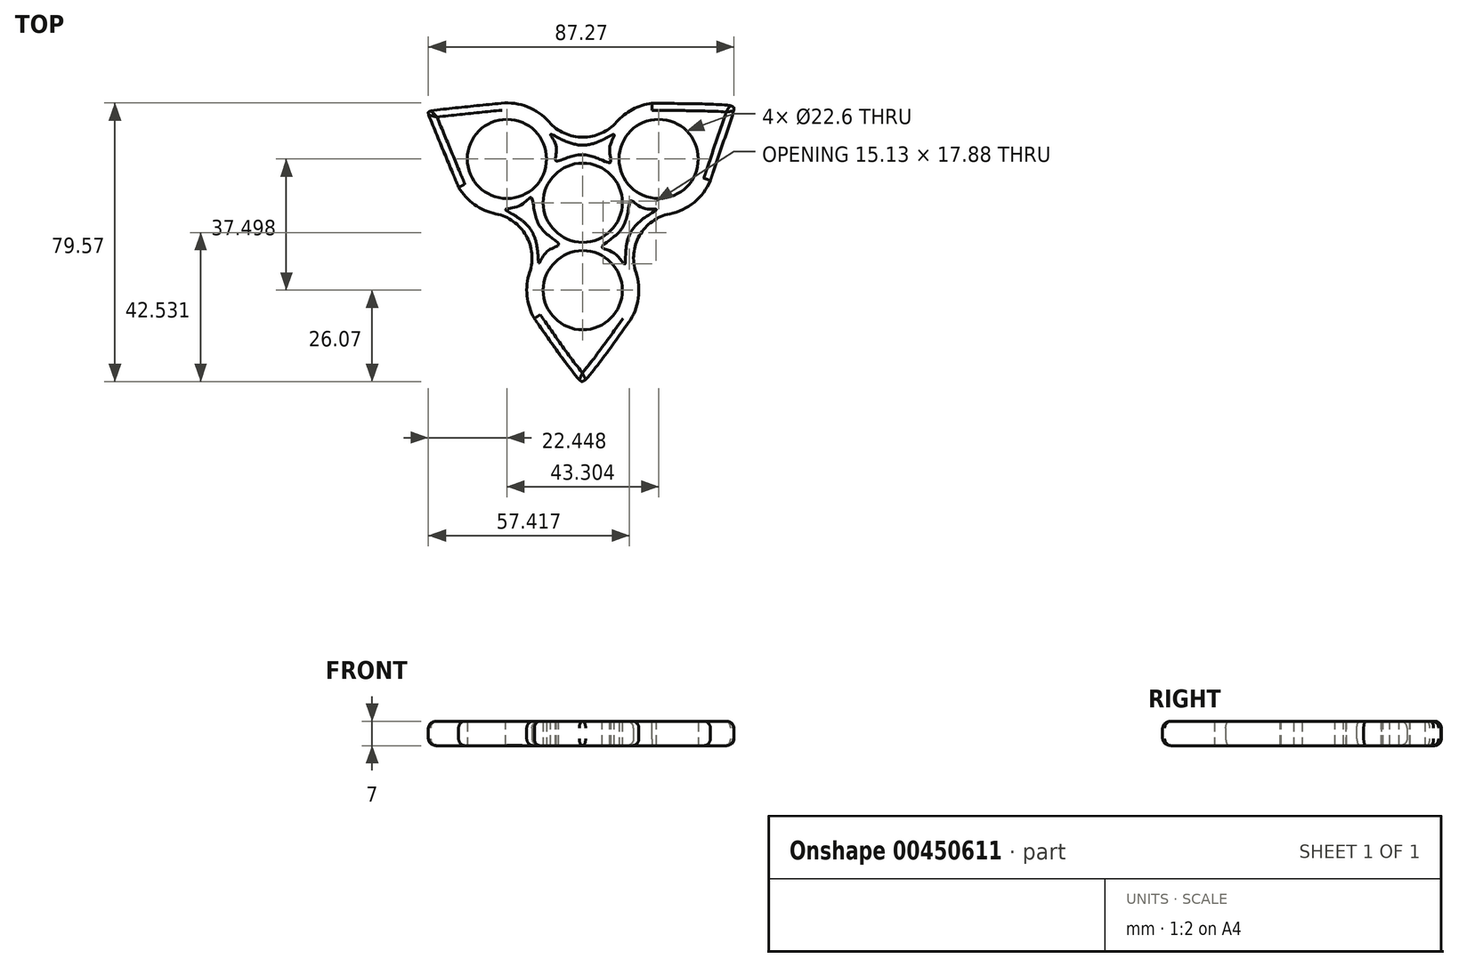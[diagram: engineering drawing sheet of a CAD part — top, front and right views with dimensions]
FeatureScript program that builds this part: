
annotation { "Feature Type Name" : "Feature", "Feature Type Description" : "" }
export const myFeature = defineFeature(function(context is Context, id is Id, definition is map)
    precondition{}
    {
        {
            var Q0;
            Q0=qCreatedBy(makeId("Top.planeOp"),FACE);
            var sketch = newSketch(context, id + "F0", { "sketchPlane" : qUnion([Q0])});
            skCircle(sketch, "E0", {"center": v(0, 0) * mm, "radius": 25 * mm});
            skCircle(sketch, "E1", {"center": v(0, 0) * mm, "radius": 11.3 * mm});
            skCircle(sketch, "E2", {"center": v(21.65, 12.5) * mm, "radius": 11.3 * mm});
            skCircle(sketch, "E3", {"center": v(-21.65, 12.5) * mm, "radius": 11.3 * mm});
            skCircle(sketch, "E4", {"center": v(0, -25) * mm, "radius": 11.3 * mm});
            skCircle(sketch, "E5", {"center": v(21.65, 12.5) * mm, "radius": 16 * mm});
            skCircle(sketch, "E6", {"center": v(-21.65, 12.5) * mm, "radius": 16 * mm});
            skCircle(sketch, "E7", {"center": v(0, -25) * mm, "radius": 16 * mm});
            skArc(sketch, "E8", {"start": v(-9.64, 23.07) * mm, "mid": v(0, 18.7) * mm, "end": v(9.64, 23.07) * mm});
            skArc(sketch, "E9", {"start": v(-15.16, -19.88) * mm, "mid": v(-16.2, -9.36) * mm, "end": v(-24.8, -3.2) * mm});
            skArc(sketch, "E10", {"start": v(24.8, -3.2) * mm, "mid": v(16.2, -9.36) * mm, "end": v(15.16, -19.88) * mm});
            skFitSpline(sketch, "E11", {"points": [v(-35.44, 4.38) * mm, v(-44.09, 25.63) * mm, v(-23.28, 28.41) * mm], "startDerivative": vector(-46.1, 111.22) * mm, "endDerivative": vector(124.83, 12.76) * mm});
            skFitSpline(sketch, "E12", {"points": [v(19.7, 28.38) * mm, v(43.05, 27.27) * mm, v(36.41, 6.32) * mm], "startDerivative": vector(126.76, -0.4) * mm, "endDerivative": vector(-40.32, -120.34) * mm});
            skFitSpline(sketch, "E13", {"points": [v(-13.83, -33.05) * mm, v(0, -51) * mm, v(13.08, -34.21) * mm], "startDerivative": vector(77.66, -112.58) * mm, "endDerivative": vector(73.36, 104.16) * mm});
            skFitSpline(sketch, "E14", {"points": [v(-9.15, 19.56) * mm, v(-7.58, 15.99) * mm, v(-7.67, 11.98) * mm, v(0, 13.72) * mm, v(7.85, 11.46) * mm, v(7.67, 15.55) * mm, v(8.9, 19.47) * mm, v(0, 16.42) * mm, v(-9.15, 19.56) * mm]});
            skFitSpline(sketch, "E15", {"points": [v(21.04, -1.96) * mm, v(17.17, -1.53) * mm, v(13.74, 0.55) * mm, v(11.41, -6.96) * mm, v(5.53, -12.62) * mm, v(9.16, -14.52) * mm, v(11.95, -17.54) * mm, v(13.75, -8.31) * mm, v(21.04, -1.96) * mm]});
            skFitSpline(sketch, "E16", {"points": [v(-12.51, -17.25) * mm, v(-10.33, -14.02) * mm, v(-6.9, -11.95) * mm, v(-12.46, -6.4) * mm, v(-14.73, 1.44) * mm, v(-18.1, -0.89) * mm, v(-22.07, -1.95) * mm, v(-14.74, -7.84) * mm, v(-12.51, -17.25) * mm]});
            skSolve(sketch);
        }
        {
            var Q0;
            {var subQ4=sQuery(id+"F0.wireOp",EDGE,"E6");var subQ5=sQuery(id+"F0.wireOp",EDGE,"E1");var subQ6=makeQuery(id+"F0.imprint","INTERSECT",VERTEX,{"disambiguationData":[OD(0.0)],"derivedFrom":[subQ5,subQ4]});Q0=makeQuery(id+"F0.imprint","IMPRINT",FACE,{"disambiguationData":[TD([[makeQuery(id+"F0.imprint","IMPRINT",EDGE,{"disambiguationData":[TD([[subQ6,-1.0]])],"derivedFrom":subQ5}),-1.0]])]});}
            var Q1;
            {var subQ0=sQuery(id+"F0.wireOp",EDGE,"E5");var subQ1=sQuery(id+"F0.wireOp",EDGE,"E1");var subQ2=makeQuery(id+"F0.imprint","INTERSECT",VERTEX,{"disambiguationData":[OD(0.0)],"derivedFrom":[subQ1,subQ0]});Q1=makeQuery(id+"F0.imprint","IMPRINT",FACE,{"disambiguationData":[TD([[makeQuery(id+"F0.imprint","IMPRINT",EDGE,{"disambiguationData":[TD([[subQ2,-1.0]])],"derivedFrom":subQ1}),-1.0]])]});}
            var Q2;
            {var subQ4=sQuery(id+"F0.wireOp",EDGE,"E5");var subQ5=sQuery(id+"F0.wireOp",EDGE,"E1");var subQ6=makeQuery(id+"F0.imprint","INTERSECT",VERTEX,{"disambiguationData":[OD(0.0)],"derivedFrom":[subQ5,subQ4]});Q2=makeQuery(id+"F0.imprint","IMPRINT",FACE,{"disambiguationData":[TD([[makeQuery(id+"F0.imprint","IMPRINT",EDGE,{"disambiguationData":[TD([[subQ6,1.0]])],"derivedFrom":subQ5}),-1.0]])]});}
            var Q3;
            {var subQ1=sQuery(id+"F0.wireOp",EDGE,"E0");var subQ3=sQuery(id+"F0.wireOp",EDGE,"E2");var subQ4=makeQuery(id+"F0.imprint","INTERSECT",VERTEX,{"disambiguationData":[OD(0.0)],"derivedFrom":[subQ1,subQ3]});Q3=makeQuery(id+"F0.imprint","IMPRINT",FACE,{"disambiguationData":[TD([[makeQuery(id+"F0.imprint","IMPRINT",EDGE,{"disambiguationData":[TD([[subQ4,1.0]])],"derivedFrom":subQ3}),-1.0]])]});}
            var Q4;
            {var subQ0=sQuery(id+"F0.wireOp",EDGE,"E5");var subQ1=sQuery(id+"F0.wireOp",EDGE,"E1");var subQ2=makeQuery(id+"F0.imprint","INTERSECT",VERTEX,{"disambiguationData":[OD(1.0)],"derivedFrom":[subQ1,subQ0]});Q4=makeQuery(id+"F0.imprint","IMPRINT",FACE,{"disambiguationData":[TD([[makeQuery(id+"F0.imprint","IMPRINT",EDGE,{"disambiguationData":[TD([[subQ2,1.0]])],"derivedFrom":subQ1}),-1.0]])]});}
            var Q5;
            {var subQ0=sQuery(id+"F0.wireOp",EDGE,"E7");var subQ1=sQuery(id+"F0.wireOp",EDGE,"E1");var subQ2=makeQuery(id+"F0.imprint","INTERSECT",VERTEX,{"disambiguationData":[OD(0.0)],"derivedFrom":[subQ1,subQ0]});Q5=makeQuery(id+"F0.imprint","IMPRINT",FACE,{"disambiguationData":[TD([[makeQuery(id+"F0.imprint","IMPRINT",EDGE,{"disambiguationData":[TD([[subQ2,-1.0]])],"derivedFrom":subQ1}),-1.0]])]});}
            var Q6;
            {var subQ0=sQuery(id+"F0.wireOp",EDGE,"E6");var subQ1=sQuery(id+"F0.wireOp",EDGE,"E1");var subQ2=makeQuery(id+"F0.imprint","INTERSECT",VERTEX,{"disambiguationData":[OD(1.0)],"derivedFrom":[subQ1,subQ0]});Q6=makeQuery(id+"F0.imprint","IMPRINT",FACE,{"disambiguationData":[TD([[makeQuery(id+"F0.imprint","IMPRINT",EDGE,{"disambiguationData":[TD([[subQ2,-1.0]])],"derivedFrom":subQ1}),-1.0]])]});}
            var Q7;
            {var subQ1=sQuery(id+"F0.wireOp",EDGE,"E0");var subQ3=sQuery(id+"F0.wireOp",EDGE,"E3");var subQ4=makeQuery(id+"F0.imprint","INTERSECT",VERTEX,{"disambiguationData":[OD(0.0)],"derivedFrom":[subQ1,subQ3]});Q7=makeQuery(id+"F0.imprint","IMPRINT",FACE,{"disambiguationData":[TD([[makeQuery(id+"F0.imprint","IMPRINT",EDGE,{"disambiguationData":[TD([[subQ4,-1.0]])],"derivedFrom":subQ3}),-1.0]])]});}
            var Q8;
            {var subQ1=sQuery(id+"F0.wireOp",EDGE,"E0");var subQ3=sQuery(id+"F0.wireOp",EDGE,"E4");var subQ4=makeQuery(id+"F0.imprint","INTERSECT",VERTEX,{"disambiguationData":[OD(0.0)],"derivedFrom":[subQ1,subQ3]});Q8=makeQuery(id+"F0.imprint","IMPRINT",FACE,{"disambiguationData":[TD([[makeQuery(id+"F0.imprint","IMPRINT",EDGE,{"disambiguationData":[TD([[subQ4,-1.0]])],"derivedFrom":subQ3}),-1.0]])]});}
            var Q9;
            {var subQ0=sQuery(id+"F0.wireOp",EDGE,"E11");var subQ1=sQuery(id+"F0.wireOp",EDGE,"E6");var subQ2=makeQuery(id+"F0.imprint","INTERSECT",VERTEX,{"disambiguationData":[OD(2.0)],"derivedFrom":[subQ1,subQ0]});Q9=makeQuery(id+"F0.imprint","IMPRINT",FACE,{"disambiguationData":[TD([[makeQuery(id+"F0.imprint","IMPRINT",EDGE,{"disambiguationData":[TD([[subQ2,-1.0]])],"derivedFrom":subQ1}),-1.0]])]});}
            var Q10;
            {var subQ0=sQuery(id+"F0.wireOp",EDGE,"E12");var subQ1=sQuery(id+"F0.wireOp",EDGE,"E5");var subQ2=makeQuery(id+"F0.imprint","INTERSECT",VERTEX,{"disambiguationData":[OD(2.0)],"derivedFrom":[subQ1,subQ0]});Q10=makeQuery(id+"F0.imprint","IMPRINT",FACE,{"disambiguationData":[TD([[makeQuery(id+"F0.imprint","IMPRINT",EDGE,{"disambiguationData":[TD([[subQ2,1.0]])],"derivedFrom":subQ1}),-1.0]])]});}
            var Q11;
            {var subQ0=sQuery(id+"F0.wireOp",EDGE,"E11");var subQ1=sQuery(id+"F0.wireOp",EDGE,"E6");var subQ2=makeQuery(id+"F0.imprint","INTERSECT",VERTEX,{"disambiguationData":[OD(1.0)],"derivedFrom":[subQ1,subQ0]});Q11=makeQuery(id+"F0.imprint","IMPRINT",FACE,{"disambiguationData":[TD([[makeQuery(id+"F0.imprint","IMPRINT",EDGE,{"disambiguationData":[TD([[subQ2,-1.0]])],"derivedFrom":subQ1}),-1.0]])]});}
            var Q12;
            {var subQ0=sQuery(id+"F0.wireOp",EDGE,"E13");var subQ1=sQuery(id+"F0.wireOp",EDGE,"E7");var subQ2=makeQuery(id+"F0.imprint","INTERSECT",VERTEX,{"disambiguationData":[OD(1.0)],"derivedFrom":[subQ1,subQ0]});Q12=makeQuery(id+"F0.imprint","IMPRINT",FACE,{"disambiguationData":[TD([[makeQuery(id+"F0.imprint","IMPRINT",EDGE,{"disambiguationData":[TD([[subQ2,1.0]])],"derivedFrom":subQ1}),-1.0]])]});}
            var Q13;
            {var subQ0=sQuery(id+"F0.wireOp",EDGE,"E8");Q13=makeQuery(id+"F0.imprint","IMPRINT",FACE,{"disambiguationData":[TD([[makeQuery(id+"F0.imprint","IMPRINT",EDGE,{"derivedFrom":subQ0}),-1.0]])]});}
            var Q14;
            {var subQ0=sQuery(id+"F0.wireOp",EDGE,"E10");Q14=makeQuery(id+"F0.imprint","IMPRINT",FACE,{"disambiguationData":[TD([[makeQuery(id+"F0.imprint","IMPRINT",EDGE,{"derivedFrom":subQ0}),-1.0]])]});}
            var Q15;
            {var subQ0=sQuery(id+"F0.wireOp",EDGE,"E9");Q15=makeQuery(id+"F0.imprint","IMPRINT",FACE,{"disambiguationData":[TD([[makeQuery(id+"F0.imprint","IMPRINT",EDGE,{"derivedFrom":subQ0}),-1.0]])]});}
            extrude(context, id + "F1", {"entities" : qUnion([Q0, Q1, Q2, Q3, Q4, Q5, Q6, Q7, Q8, Q9, Q10, Q11, Q12, Q13, Q14, Q15]), "depth" : 7 * mm});
        }
        {
            var Q0;
            Q0=makeQuery(id+"F1.opExtrude","CAP_EDGE",EDGE,{"disambiguationData":[OSD([sQuery(id+"F0.wireOp",EDGE,"E13")])],"isStart":false});
            var Q1;
            {var subQ0=sQuery(id+"F0.wireOp",EDGE,"E7");Q1=makeQuery(id+"F1.opExtrude","CAP_EDGE",EDGE,{"disambiguationData":[OSD([subQ0]),TDD([makeQuery(id+"F0.imprint","IMPRINT",EDGE,{"disambiguationData":[TD([[makeQuery(id+"F0.imprint","INTERSECT",VERTEX,{"disambiguationData":[OD(1.0)],"derivedFrom":[subQ0,sQuery(id+"F0.wireOp",EDGE,"E13")]}),-1.0]])],"derivedFrom":subQ0})])],"isStart":false});}
            var Q2;
            Q2=makeQuery(id+"F1.opExtrude","CAP_EDGE",EDGE,{"disambiguationData":[OSD([sQuery(id+"F0.wireOp",EDGE,"E10")])],"isStart":false});
            var Q3;
            {var subQ0=sQuery(id+"F0.wireOp",EDGE,"E5");Q3=makeQuery(id+"F1.opExtrude","CAP_EDGE",EDGE,{"disambiguationData":[OSD([subQ0]),TDD([makeQuery(id+"F0.imprint","IMPRINT",EDGE,{"disambiguationData":[TD([[makeQuery(id+"F0.imprint","INTERSECT",VERTEX,{"disambiguationData":[OD(1.0)],"derivedFrom":[subQ0,sQuery(id+"F0.wireOp",EDGE,"E12")]}),1.0]])],"derivedFrom":subQ0})])],"isStart":false});}
            var Q4;
            Q4=makeQuery(id+"F1.opExtrude","CAP_EDGE",EDGE,{"disambiguationData":[OSD([sQuery(id+"F0.wireOp",EDGE,"E12")])],"isStart":false});
            var Q5;
            {var subQ0=sQuery(id+"F0.wireOp",EDGE,"E5");Q5=makeQuery(id+"F1.opExtrude","CAP_EDGE",EDGE,{"disambiguationData":[OSD([subQ0]),TDD([makeQuery(id+"F0.imprint","IMPRINT",EDGE,{"disambiguationData":[TD([[makeQuery(id+"F0.imprint","INTERSECT",VERTEX,{"disambiguationData":[OD(0.0)],"derivedFrom":[subQ0,sQuery(id+"F0.wireOp",EDGE,"E12")]}),-1.0]])],"derivedFrom":subQ0})])],"isStart":false});}
            var Q6;
            Q6=makeQuery(id+"F1.opExtrude","CAP_EDGE",EDGE,{"disambiguationData":[OSD([sQuery(id+"F0.wireOp",EDGE,"E8")])],"isStart":false});
            var Q7;
            {var subQ0=sQuery(id+"F0.wireOp",EDGE,"E6");Q7=makeQuery(id+"F1.opExtrude","CAP_EDGE",EDGE,{"disambiguationData":[OSD([subQ0]),TDD([makeQuery(id+"F0.imprint","IMPRINT",EDGE,{"disambiguationData":[TD([[makeQuery(id+"F0.imprint","INTERSECT",VERTEX,{"disambiguationData":[OD(1.0)],"derivedFrom":[subQ0,sQuery(id+"F0.wireOp",EDGE,"E11")]}),1.0]])],"derivedFrom":subQ0})])],"isStart":false});}
            var Q8;
            Q8=makeQuery(id+"F1.opExtrude","CAP_EDGE",EDGE,{"disambiguationData":[OSD([sQuery(id+"F0.wireOp",EDGE,"E11")])],"isStart":false});
            var Q9;
            {var subQ0=sQuery(id+"F0.wireOp",EDGE,"E6");Q9=makeQuery(id+"F1.opExtrude","CAP_EDGE",EDGE,{"disambiguationData":[OSD([subQ0]),TDD([makeQuery(id+"F0.imprint","IMPRINT",EDGE,{"disambiguationData":[TD([[makeQuery(id+"F0.imprint","INTERSECT",VERTEX,{"disambiguationData":[OD(0.0)],"derivedFrom":[subQ0,sQuery(id+"F0.wireOp",EDGE,"E11")]}),-1.0]])],"derivedFrom":subQ0})])],"isStart":false});}
            var Q10;
            Q10=makeQuery(id+"F1.opExtrude","CAP_EDGE",EDGE,{"disambiguationData":[OSD([sQuery(id+"F0.wireOp",EDGE,"E9")])],"isStart":false});
            var Q11;
            {var subQ0=sQuery(id+"F0.wireOp",EDGE,"E7");Q11=makeQuery(id+"F1.opExtrude","CAP_EDGE",EDGE,{"disambiguationData":[OSD([subQ0]),TDD([makeQuery(id+"F0.imprint","IMPRINT",EDGE,{"disambiguationData":[TD([[makeQuery(id+"F0.imprint","INTERSECT",VERTEX,{"disambiguationData":[OD(0.0)],"derivedFrom":[subQ0,sQuery(id+"F0.wireOp",EDGE,"E13")]}),1.0]])],"derivedFrom":subQ0})])],"isStart":false});}
            fillet(context, id + "F2", {"entities" : qUnion([Q0, Q1, Q2, Q3, Q4, Q5, Q6, Q7, Q8, Q9, Q10, Q11]), "radius" : 2 * mm, "tangentPropagation" : true, "allowEdgeOverflow" : false});
        }
        {
            var Q0;
            Q0=makeQuery(id+"F1.opExtrude","CAP_EDGE",EDGE,{"disambiguationData":[OSD([sQuery(id+"F0.wireOp",EDGE,"E13")])],"isStart":true});
            var Q1;
            {var subQ0=sQuery(id+"F0.wireOp",EDGE,"E7");Q1=makeQuery(id+"F1.opExtrude","CAP_EDGE",EDGE,{"disambiguationData":[OSD([subQ0]),TDD([makeQuery(id+"F0.imprint","IMPRINT",EDGE,{"disambiguationData":[TD([[makeQuery(id+"F0.imprint","INTERSECT",VERTEX,{"disambiguationData":[OD(0.0)],"derivedFrom":[subQ0,sQuery(id+"F0.wireOp",EDGE,"E13")]}),1.0]])],"derivedFrom":subQ0})])],"isStart":true});}
            var Q2;
            Q2=makeQuery(id+"F1.opExtrude","CAP_EDGE",EDGE,{"disambiguationData":[OSD([sQuery(id+"F0.wireOp",EDGE,"E9")])],"isStart":true});
            var Q3;
            {var subQ0=sQuery(id+"F0.wireOp",EDGE,"E6");Q3=makeQuery(id+"F1.opExtrude","CAP_EDGE",EDGE,{"disambiguationData":[OSD([subQ0]),TDD([makeQuery(id+"F0.imprint","IMPRINT",EDGE,{"disambiguationData":[TD([[makeQuery(id+"F0.imprint","INTERSECT",VERTEX,{"disambiguationData":[OD(0.0)],"derivedFrom":[subQ0,sQuery(id+"F0.wireOp",EDGE,"E11")]}),-1.0]])],"derivedFrom":subQ0})])],"isStart":true});}
            var Q4;
            Q4=makeQuery(id+"F1.opExtrude","CAP_EDGE",EDGE,{"disambiguationData":[OSD([sQuery(id+"F0.wireOp",EDGE,"E11")])],"isStart":true});
            var Q5;
            {var subQ0=sQuery(id+"F0.wireOp",EDGE,"E6");Q5=makeQuery(id+"F1.opExtrude","CAP_EDGE",EDGE,{"disambiguationData":[OSD([subQ0]),TDD([makeQuery(id+"F0.imprint","IMPRINT",EDGE,{"disambiguationData":[TD([[makeQuery(id+"F0.imprint","INTERSECT",VERTEX,{"disambiguationData":[OD(1.0)],"derivedFrom":[subQ0,sQuery(id+"F0.wireOp",EDGE,"E11")]}),1.0]])],"derivedFrom":subQ0})])],"isStart":true});}
            var Q6;
            Q6=makeQuery(id+"F1.opExtrude","CAP_EDGE",EDGE,{"disambiguationData":[OSD([sQuery(id+"F0.wireOp",EDGE,"E8")])],"isStart":true});
            var Q7;
            {var subQ0=sQuery(id+"F0.wireOp",EDGE,"E5");Q7=makeQuery(id+"F1.opExtrude","CAP_EDGE",EDGE,{"disambiguationData":[OSD([subQ0]),TDD([makeQuery(id+"F0.imprint","IMPRINT",EDGE,{"disambiguationData":[TD([[makeQuery(id+"F0.imprint","INTERSECT",VERTEX,{"disambiguationData":[OD(0.0)],"derivedFrom":[subQ0,sQuery(id+"F0.wireOp",EDGE,"E12")]}),-1.0]])],"derivedFrom":subQ0})])],"isStart":true});}
            var Q8;
            {var subQ0=sQuery(id+"F0.wireOp",EDGE,"E5");Q8=makeQuery(id+"F1.opExtrude","CAP_EDGE",EDGE,{"disambiguationData":[OSD([subQ0]),TDD([makeQuery(id+"F0.imprint","IMPRINT",EDGE,{"disambiguationData":[TD([[makeQuery(id+"F0.imprint","INTERSECT",VERTEX,{"disambiguationData":[OD(1.0)],"derivedFrom":[subQ0,sQuery(id+"F0.wireOp",EDGE,"E12")]}),1.0]])],"derivedFrom":subQ0})])],"isStart":true});}
            var Q9;
            Q9=makeQuery(id+"F1.opExtrude","CAP_EDGE",EDGE,{"disambiguationData":[OSD([sQuery(id+"F0.wireOp",EDGE,"E10")])],"isStart":true});
            var Q10;
            {var subQ0=sQuery(id+"F0.wireOp",EDGE,"E7");Q10=makeQuery(id+"F1.opExtrude","CAP_EDGE",EDGE,{"disambiguationData":[OSD([subQ0]),TDD([makeQuery(id+"F0.imprint","IMPRINT",EDGE,{"disambiguationData":[TD([[makeQuery(id+"F0.imprint","INTERSECT",VERTEX,{"disambiguationData":[OD(1.0)],"derivedFrom":[subQ0,sQuery(id+"F0.wireOp",EDGE,"E13")]}),-1.0]])],"derivedFrom":subQ0})])],"isStart":true});}
            var Q11;
            Q11=makeQuery(id+"F1.opExtrude","CAP_EDGE",EDGE,{"disambiguationData":[OSD([sQuery(id+"F0.wireOp",EDGE,"E12")])],"isStart":true});
            fillet(context, id + "F3", {"entities" : qUnion([Q0, Q1, Q2, Q3, Q4, Q5, Q6, Q7, Q8, Q9, Q10, Q11]), "radius" : 2 * mm, "tangentPropagation" : true, "allowEdgeOverflow" : false});
        }
    });
